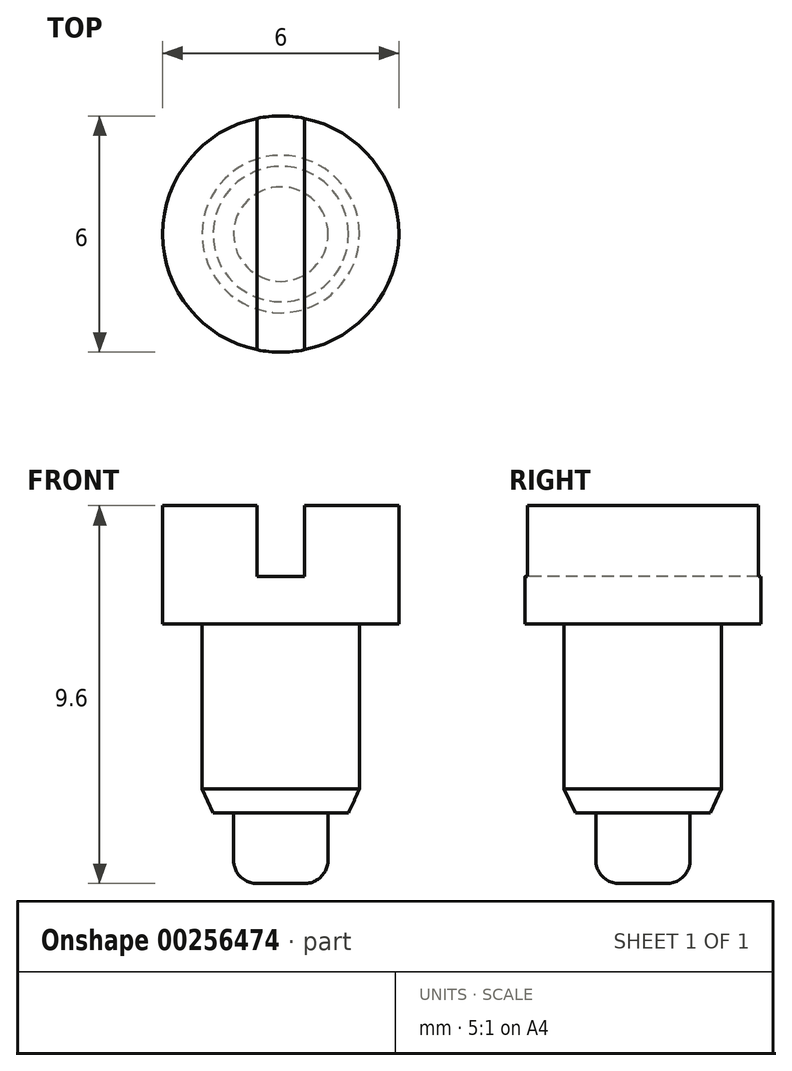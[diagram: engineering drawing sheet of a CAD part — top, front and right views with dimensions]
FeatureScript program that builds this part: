
annotation { "Feature Type Name" : "Feature", "Feature Type Description" : "" }
export const myFeature = defineFeature(function(context is Context, id is Id, definition is map)
    precondition{}
    {
        {
            var Q0;
            Q0=qCreatedBy(makeId("Front.planeOp"),FACE);
            var sketch = newSketch(context, id + "F0", { "sketchPlane" : qUnion([Q0])});
            skLineSegment(sketch, "E0", {"start": v(0, 0) * mm, "end": v(0.2, 0) * mm});
            skLineSegment(sketch, "E1", {"start": v(0.4, 0.2) * mm, "end": v(0.4, 0.6) * mm});
            skLineSegment(sketch, "E2", {"start": v(0.4, 0.6) * mm, "end": v(0.57, 0.6) * mm});
            skLineSegment(sketch, "E3", {"start": v(0.57, 0.6) * mm, "end": v(0.67, 0.8) * mm});
            skLineSegment(sketch, "E4", {"start": v(0.67, 0.8) * mm, "end": v(0.67, 2.2) * mm});
            skLineSegment(sketch, "E5", {"start": v(0.67, 2.2) * mm, "end": v(1, 2.2) * mm});
            skLineSegment(sketch, "E6", {"start": v(1, 2.2) * mm, "end": v(1, 3.2) * mm});
            skLineSegment(sketch, "E7", {"start": v(1, 3.2) * mm, "end": v(0, 3.2) * mm});
            skLineSegment(sketch, "E8", {"start": v(0, 3.2) * mm, "end": v(0, 0) * mm});
            skPoint(sketch, "E9.visualSharp", {"position": v(0.4, 0) * mm});
            skArc(sketch, "E9.filletArc", {"start": v(0.2, 0) * mm, "mid": v(0.34, 0.06) * mm, "end": v(0.4, 0.2) * mm});
            skSolve(sketch);
        }
        {
            var Q0;
            Q0=makeQuery(id+"F0.imprint","IMPRINT",FACE,{"disambiguationData":[TD([[makeQuery(id+"F0.imprint","IMPRINT",EDGE,{"derivedFrom":sQuery(id+"F0.wireOp",EDGE,"E0")}),1.0]])]});
            var Q1;
            Q1=sQuery(id+"F0.wireOp",EDGE,"E8");
            revolve(context, id + "F1", {"entities" : qUnion([Q0]), "axis" : qUnion([Q1]), "revolveType" : RevolveType.FULL});
        }
        {
            var Q0;
            Q0=makeQuery(id+"F1.opRevolve","SWEPT_FACE",FACE,{"disambiguationData":[OSD([sQuery(id+"F0.wireOp",EDGE,"E7")])]});
            var sketch = newSketch(context, id + "F2", { "sketchPlane" : qUnion([Q0])});
            skLineSegment(sketch, "E10", {"start": v(-0.2, 0.98) * mm, "end": v(-0.2, -0.98) * mm});
            skLineSegment(sketch, "E11", {"start": v(0.2, -0.98) * mm, "end": v(0.2, 0.98) * mm});
            skSolve(sketch);
        }
        {
            var Q0;
            {var subQ2=sQuery(id+"F2.wireOp",EDGE,"E10");Q0=makeQuery(id+"F2.imprint","IMPRINT",FACE,{"disambiguationData":[TD([[makeQuery(id+"F2.imprint","IMPRINT",EDGE,{"derivedFrom":subQ2}),1.0]])]});}
            extrude(context, id + "F3", {"entities" : qUnion([Q0]), "operationType" : NewBodyOperationType.REMOVE, "oppositeDirection" : true, "depth" : 0.6 * mm});
        }
        {
            var Q0;
            Q0=makeQuery(id+"F1.opRevolve","SWEPT_BODY",BODY,{"disambiguationData":[OSD([sQuery(id+"F0.wireOp",EDGE,"E0"),sQuery(id+"F0.wireOp",EDGE,"E1"),sQuery(id+"F0.wireOp",EDGE,"E2"),sQuery(id+"F0.wireOp",EDGE,"E3"),sQuery(id+"F0.wireOp",EDGE,"E4"),sQuery(id+"F0.wireOp",EDGE,"E5"),sQuery(id+"F0.wireOp",EDGE,"E6"),sQuery(id+"F0.wireOp",EDGE,"E7"),sQuery(id+"F0.wireOp",EDGE,"E8"),sQuery(id+"F0.wireOp",EDGE,"E9.filletArc")])]});
            var Q1;
            Q1=qCreatedBy(makeId("Origin.pointOp"),VERTEX);
            transform(context, id + "F4", {"entities" : qUnion([Q0]), "transformType" : TransformType.SCALE_UNIFORMLY, "scale" : 3, "makeCopy" : false, "scalePoint" : qUnion([Q1])});
        }
    });
